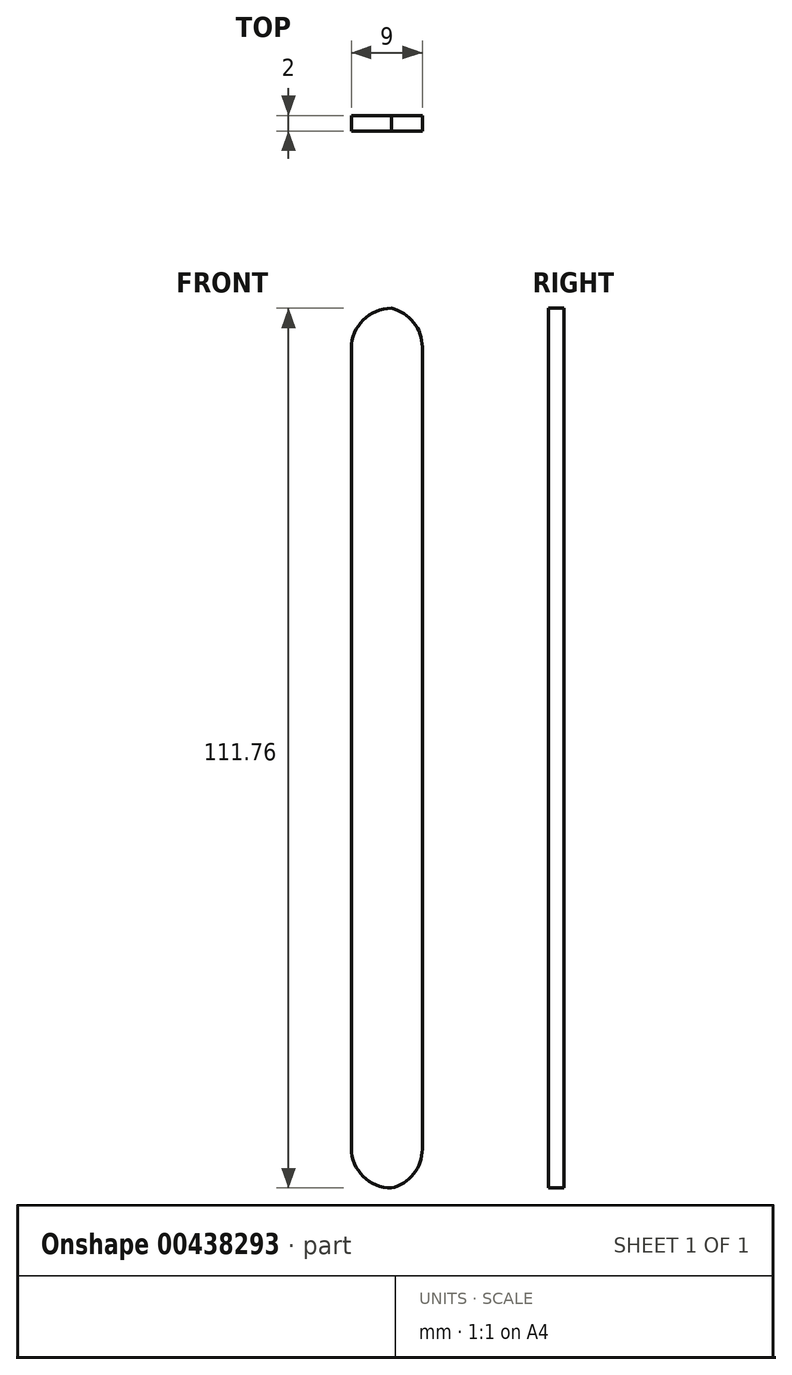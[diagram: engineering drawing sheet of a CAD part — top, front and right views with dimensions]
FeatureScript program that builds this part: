
annotation { "Feature Type Name" : "Feature", "Feature Type Description" : "" }
export const myFeature = defineFeature(function(context is Context, id is Id, definition is map)
    precondition{}
    {
        {
            var Q0;
            Q0=qCreatedBy(makeId("Front.planeOp"),FACE);
            var sketch = newSketch(context, id + "F0", { "sketchPlane" : qUnion([Q0])});
            skLineSegment(sketch, "E0.bottom", {"start": v(-9, 63.63) * mm, "end": v(0, 63.63) * mm});
            skLineSegment(sketch, "E0.top", {"start": v(-9, -48.13) * mm, "end": v(0, -48.13) * mm});
            skLineSegment(sketch, "E0.left", {"start": v(-9, 63.63) * mm, "end": v(-9, -48.13) * mm});
            skLineSegment(sketch, "E0.right", {"start": v(0, 63.63) * mm, "end": v(0, -48.13) * mm});
            skSolve(sketch);
        }
        {
            var Q0;
            Q0=makeQuery(id+"F0.imprint","IMPRINT",FACE,{"disambiguationData":[TD([[makeQuery(id+"F0.imprint","IMPRINT",EDGE,{"derivedFrom":sQuery(id+"F0.wireOp",EDGE,"E0.bottom")}),-1.0]])]});
            extrude(context, id + "F1", {"entities" : qUnion([Q0]), "depth" : 2 * mm});
        }
        {
            var Q0;
            Q0=makeQuery(id+"F1.opExtrude","SWEPT_EDGE",EDGE,{"disambiguationData":[OSD([sQuery(id+"F0.wireOp",EDGE,"E0.bottom"),sQuery(id+"F0.wireOp",EDGE,"E0.left")])]});
            fillet(context, id + "F2", {"entities" : qUnion([Q0]), "radius" : 5.08 * mm, "tangentPropagation" : true, "allowEdgeOverflow" : false});
        }
        {
            var Q0;
            Q0=makeQuery(id+"F1.opExtrude","SWEPT_EDGE",EDGE,{"disambiguationData":[OSD([sQuery(id+"F0.wireOp",EDGE,"E0.bottom"),sQuery(id+"F0.wireOp",EDGE,"E0.right")])]});
            fillet(context, id + "F3", {"entities" : qUnion([Q0]), "radius" : 5.08 * mm, "tangentPropagation" : true, "allowEdgeOverflow" : false});
        }
        {
            var Q0;
            Q0=makeQuery(id+"F1.opExtrude","SWEPT_EDGE",EDGE,{"disambiguationData":[OSD([sQuery(id+"F0.wireOp",EDGE,"E0.top"),sQuery(id+"F0.wireOp",EDGE,"E0.left")])]});
            fillet(context, id + "F4", {"entities" : qUnion([Q0]), "radius" : 5.08 * mm, "tangentPropagation" : true, "allowEdgeOverflow" : false});
        }
        {
            var Q0;
            Q0=makeQuery(id+"F1.opExtrude","SWEPT_EDGE",EDGE,{"disambiguationData":[OSD([sQuery(id+"F0.wireOp",EDGE,"E0.top"),sQuery(id+"F0.wireOp",EDGE,"E0.right")])]});
            fillet(context, id + "F5", {"entities" : qUnion([Q0]), "radius" : 5.08 * mm, "tangentPropagation" : true, "allowEdgeOverflow" : false});
        }
    });
